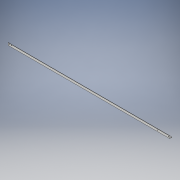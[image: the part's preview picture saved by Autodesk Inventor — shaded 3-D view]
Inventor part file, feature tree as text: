
AUTODESK INVENTOR PART (.ipt)
format: ipt  version: 2017 (Build 210142000, 142)  size: 137,216 bytes
history: native  units: in
note: dims shown in document units (in); Inventor stores cm internally (conversion verified against a paired STEP export)
features: extrude x5, sketch x5
ambient origin geometry x8: Origin, YZ Plane, XZ Plane, XY Plane, X Axis, Y Axis, Z Axis, Center Point
bodies: Solid1 (feature_tree)
feature tree (10):
  extrude  "Extrusion1"  Depth=0.128in
  extrude  "Extrusion2"  Depth=72.0in TaperAngle=0.0deg
  extrude  "Extrusion3"  Depth=0.5in
  extrude  "Extrusion4"  Depth=72.0in TaperAngle=0.0deg
  extrude  "Extrusion5"  Depth=72.0in TaperAngle=0.0deg
  sketch  "Sketch1"  dims[d2=0.128in d3=0.128in]
  sketch  "Sketch2"  dims[d4=1.0in d5=72.0in d6=0.0in]
  sketch  "Sketch3"  dims[d7=0.25in d8=0.5in]
  sketch  "Sketch4"  dims[d9=1.5in d10=72.0in d11=0.0in]
  sketch  "Sketch5"  dims[d12=0.25in d15=72.0in d16=0.0in d17=0.628in d18=10.5in d19=11.5in d20=0.628in d21=0.25in d22=0.5in d23=5.5in d24=72.0in d25=0.0in d26=0.25in d27=0.5in d28=5.5in d29=72.0in d30=0.0in]
